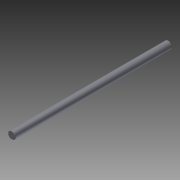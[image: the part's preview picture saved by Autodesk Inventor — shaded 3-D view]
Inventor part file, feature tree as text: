
AUTODESK INVENTOR PART (.ipt)
format: ipt  version: 2012 (Build 160160000, 160)  size: 70,144 bytes
history: native  units: in
note: dims shown in document units (in); Inventor stores cm internally (conversion verified against a paired STEP export)
features: extrude x1, chamfer x1, sketch x1
ambient origin geometry x8: Origin, YZ Plane, XZ Plane, XY Plane, X Axis, Y Axis, Z Axis, Center Point
bodies: Solid1 (feature_tree)
feature tree (3):
  extrude  "Extrusion1"  Depth=10.0in TaperAngle=0.0deg
  chamfer  "Chamfer1"  Distance=0.0197in Angle=45.0deg
  sketch  "Sketch1"  dims[d0=0.4724in d1=10.0in d2=0.0in d3=0.0197in d4=0.125in d5=45.0deg]
